# Revit family: 1176xxx Zeppo Ceiling
name_source: partatom
category: Lighting Fixtures
units: mm (PartAtom-declared; Revit-internal decimal feet)

## family parameters
Always vertical = Yes
Cut with Voids When Loaded = No
Host = Ceiling
Light Source = No
OmniClass Number = 23.80.70.11
OmniClass Title = Luminaries for Internal Lighting
Part Type = Normal
Room Calculation Point = No
Round Connector Dimension = Use Diameter
Shared = No

## types (2) — shared parameters
Manufacturer URL - Europe and Rest of World = www.astrolighting.com
Product CCT = 2700K / 3000K
zero-valued in all types: Default Elevation

## per-type parameters (varying)
| type | ADA compliant | Dimmable | Dimming Method | Driver Included | Driver Required | Efficacy (lm/w) | Electrical Class | Lamp | Length of supplied cable | Light Source Fixed | Location / IP Rating | Main Finish | Main Material | Manufacturer URL - North America | Max Drop (pendants) | Power (Watts) | Product CRI | Product Dimensions (MM) | Product Location | Product Name | Product SKU | Product URL | Product Weight (KG) | Wattage Comments |
| CE | Not Applicable | Yes | Lamp Dependent | Not Applicable | No | Lamp Dependent | 2 | E27 | Not Applicable | Yes | Bathroom / IP44 | 1176001 | Glass | https://www.astrolighting.com | Not Applicable | 12W | 80 / 90 | 235 x 300 | Ceiling | Zeppo Ceiling | 1176001 | https://www.astrolighting.com | 2 mm  [stored 0.00656168 ft] | 12W Max |
| ETL |  |  |  |  |  |  |  |  |  |  |  |  |  | us.astrolighting.com |  |  | 80/ 90 |  |  |  | 1234567 |  | 0 mm  [stored 0 ft] |  |

note: [stored X ft] marks values corroborated as IEEE doubles in the binary element streams (Revit-internal decimal feet)

## geometry (parser evidence)
native form markers: Sweep x3
no freeform markers — native parametric forms only
